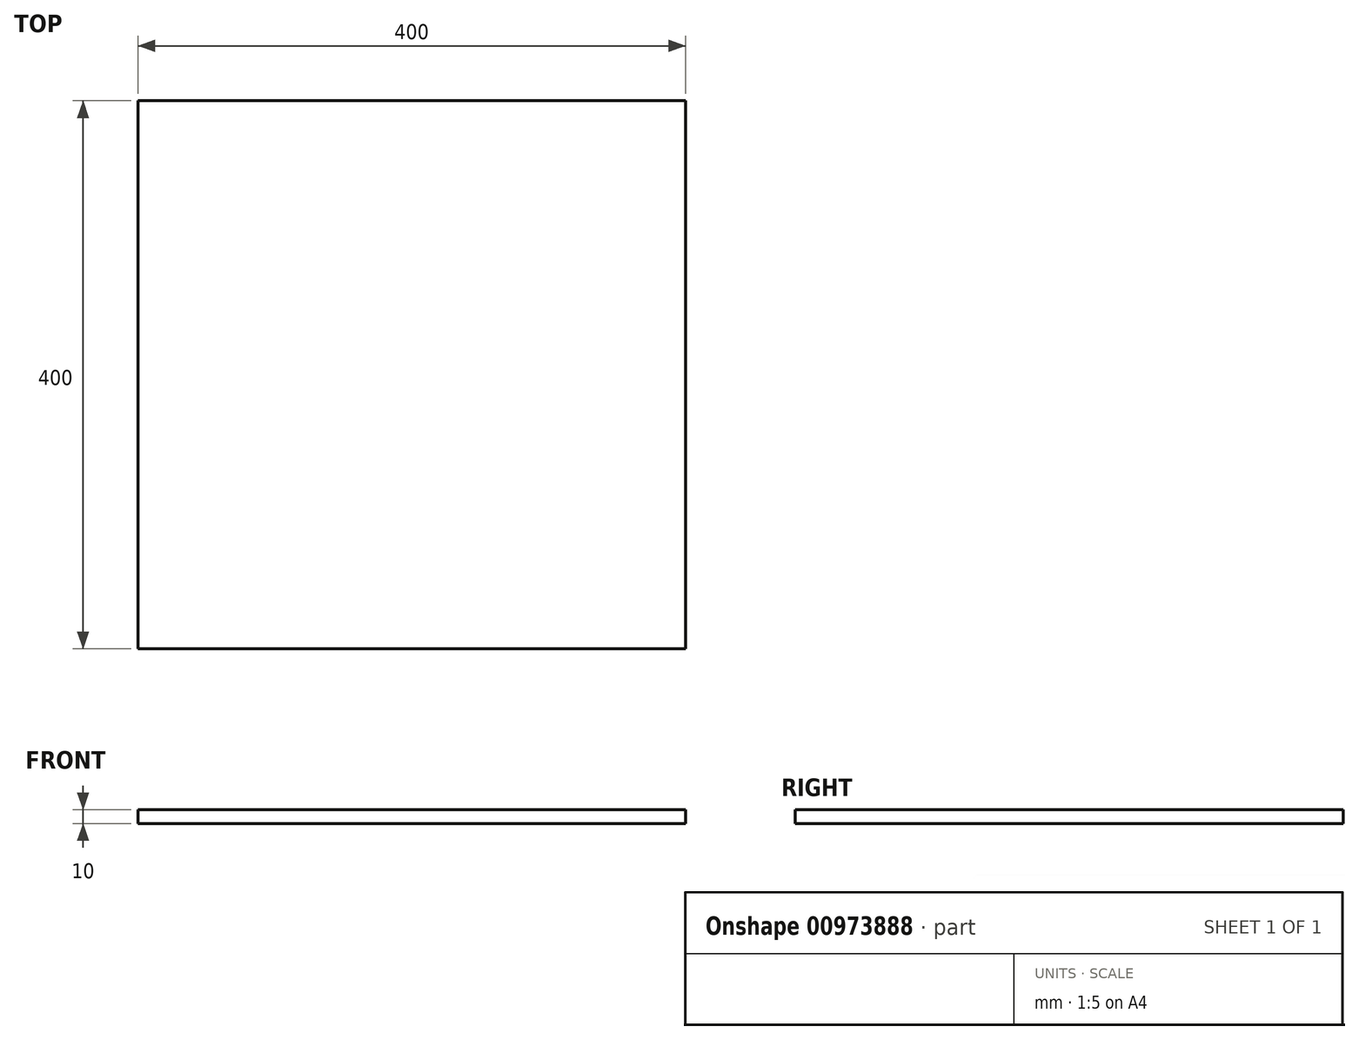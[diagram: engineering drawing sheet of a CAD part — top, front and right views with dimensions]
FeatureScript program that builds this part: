
annotation { "Feature Type Name" : "Feature", "Feature Type Description" : "" }
export const myFeature = defineFeature(function(context is Context, id is Id, definition is map)
    precondition{}
    {
        {
            var Q0;
            Q0=qCreatedBy(makeId("Top.planeOp"),FACE);
            var sketch = newSketch(context, id + "F0", { "sketchPlane" : qUnion([Q0])});
            skLineSegment(sketch, "E0.bottom", {"start": v(-200, 200) * mm, "end": v(200, 200) * mm});
            skLineSegment(sketch, "E0.top", {"start": v(-200, -200) * mm, "end": v(200, -200) * mm});
            skLineSegment(sketch, "E0.left", {"start": v(-200, 200) * mm, "end": v(-200, -200) * mm});
            skLineSegment(sketch, "E0.right", {"start": v(200, 200) * mm, "end": v(200, -200) * mm});
            skLineSegment(sketch, "E1", {"start": v(200, 200) * mm, "end": v(-200, -200) * mm, "construction": true});
            skLineSegment(sketch, "E2", {"start": v(0, 0) * mm, "end": v(200, -200) * mm, "construction": true});
            skSolve(sketch);
        }
        {
            var Q0;
            Q0 = qSketchRegion(id + "F0", true);
            extrude(context, id + "F1", {"entities" : qUnion([Q0]), "depth" : 10 * mm, "offsetDistance" : 25.4 * mm});
        }
    });
